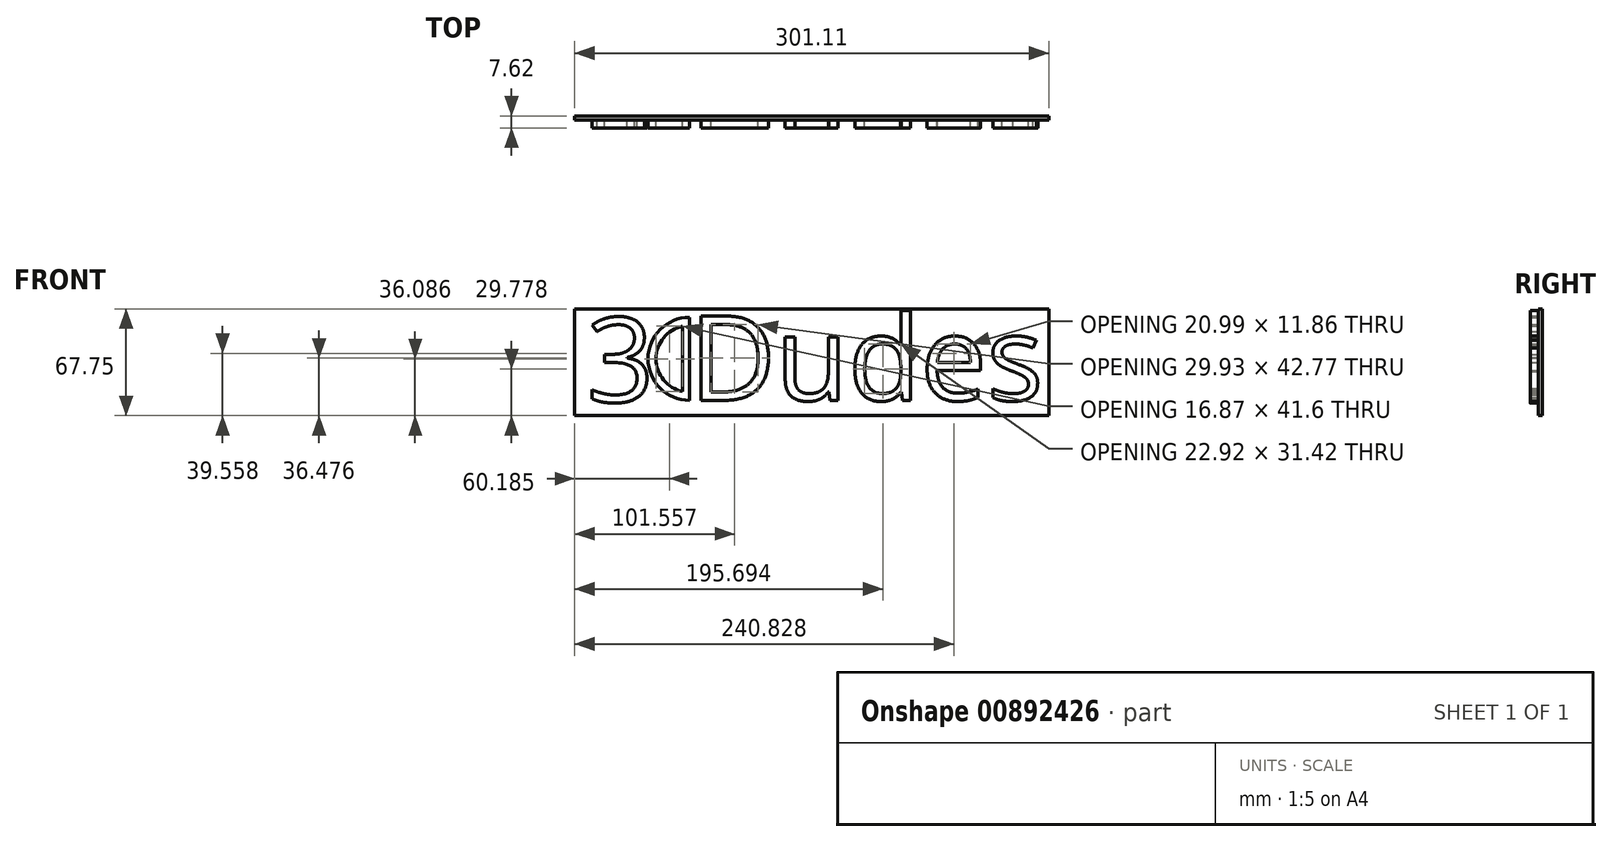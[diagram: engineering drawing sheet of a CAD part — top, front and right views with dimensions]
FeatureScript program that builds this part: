
annotation { "Feature Type Name" : "Feature", "Feature Type Description" : "" }
export const myFeature = defineFeature(function(context is Context, id is Id, definition is map)
    precondition{}
    {
        {
            var Q0;
            Q0=qCreatedBy(makeId("Front.planeOp"),FACE);
            var sketch = newSketch(context, id + "F0", { "sketchPlane" : qUnion([Q0])});
            skText(sketch, "E0", { "text": "Dudes", "fontName": "OpenSans-Regular.ttf"});
            skArc(sketch, "E1", {"start": v(-12.79, 24.5) * mm, "mid": v(-39.18, -1.9) * mm, "end": v(-12.79, -28.29) * mm});
            skLineSegment(sketch, "E2", {"start": v(-12.79, -1.9) * mm, "end": v(-12.79, -28.29) * mm});
            skLineSegment(sketch, "E3", {"start": v(-12.79, -28.29) * mm, "end": v(-12.79, 24.5) * mm});
            skText(sketch, "E4", { "text": "3", "fontName": "OpenSans-Regular.ttf"});
            skArc(sketch, "E5", {"start": v(-17.18, 18.9) * mm, "mid": v(-34.05, -1.9) * mm, "end": v(-17.18, -22.7) * mm});
            skLineSegment(sketch, "E6", {"start": v(-17.18, 18.9) * mm, "end": v(-17.18, -22.7) * mm});
            const initialGuessF0  = {"E0": [-0.01279, -0.02827, 1, 0, 0.054], "E4": [-0.07836, -0.02926, 1, 0, 0.05397]};
            skSetInitialGuess(sketch, initialGuessF0);
            skSolve(sketch);
        }
        {
            var Q0;
            Q0 = qSketchRegion(id + "F0", true);
            extrude(context, id + "F1", {"entities" : qUnion([Q0]), "depth" : 5.08 * mm, "offsetDistance" : 25.4 * mm});
        }
        {
            var Q0;
            Q0=qCreatedBy(makeId("Front.planeOp"),FACE);
            var sketch = newSketch(context, id + "F2", { "sketchPlane" : qUnion([Q0])});
            skLineSegment(sketch, "E7.bottom", {"start": v(-85.8, 29.77) * mm, "end": v(215.31, 29.77) * mm});
            skLineSegment(sketch, "E7.top", {"start": v(-85.8, -37.98) * mm, "end": v(215.31, -37.98) * mm});
            skLineSegment(sketch, "E7.left", {"start": v(-85.8, 29.77) * mm, "end": v(-85.8, -37.98) * mm});
            skLineSegment(sketch, "E7.right", {"start": v(215.31, 29.77) * mm, "end": v(215.31, -37.98) * mm});
            skSolve(sketch);
        }
        {
            var Q0;
            Q0=makeQuery(id+"F2.imprint","IMPRINT",FACE,{"disambiguationData":[TD([[makeQuery(id+"F2.imprint","IMPRINT",EDGE,{"derivedFrom":sQuery(id+"F2.wireOp",EDGE,"E7.bottom")}),-1.0]])]});
            extrude(context, id + "F3", {"entities" : qUnion([Q0]), "oppositeDirection" : true, "depth" : 2.54 * mm, "offsetDistance" : 25.4 * mm});
        }
    });
